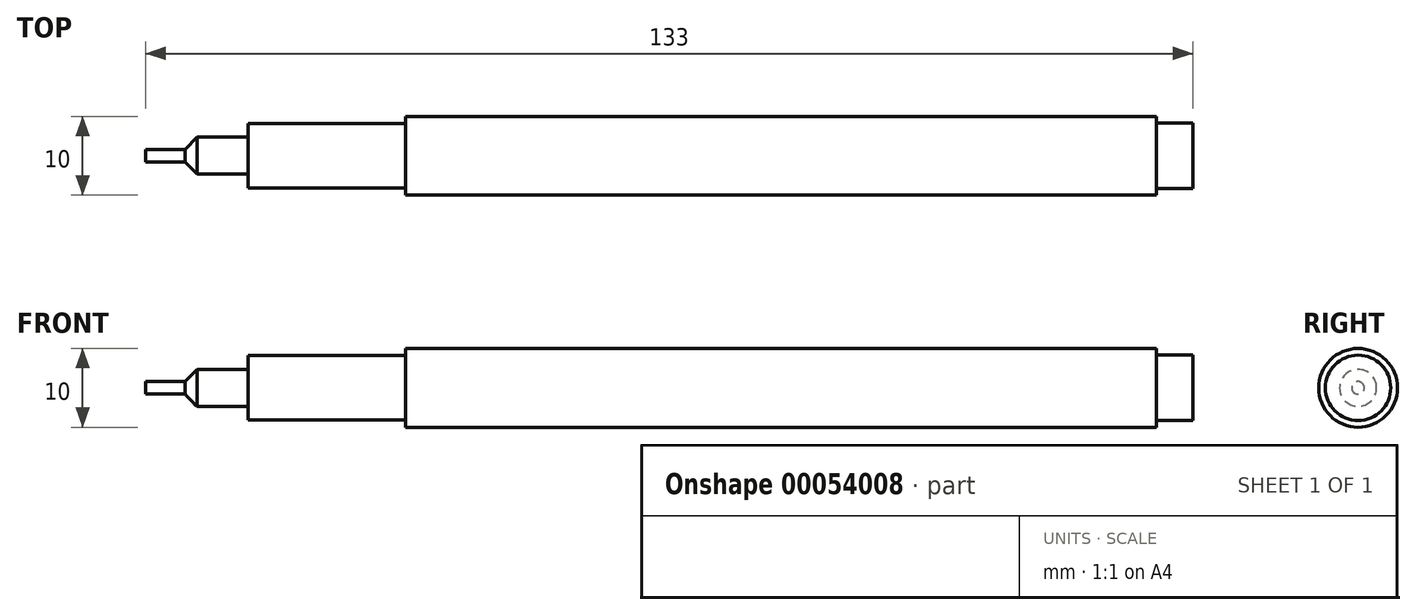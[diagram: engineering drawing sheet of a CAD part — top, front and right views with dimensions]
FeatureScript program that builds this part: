
annotation { "Feature Type Name" : "Feature", "Feature Type Description" : "" }
export const myFeature = defineFeature(function(context is Context, id is Id, definition is map)
    precondition{}
    {
        {
            var Q0;
            Q0=qCreatedBy(makeId("Top.planeOp"),FACE);
            var sketch = newSketch(context, id + "F0", { "sketchPlane" : qUnion([Q0])});
            skLineSegment(sketch, "E0", {"start": v(0, 0) * mm, "end": v(0, 0.8) * mm});
            skLineSegment(sketch, "E1", {"start": v(0, 0.8) * mm, "end": v(5, 0.8) * mm});
            skLineSegment(sketch, "E2", {"start": v(33, 4.1) * mm, "end": v(33, 5) * mm});
            skLineSegment(sketch, "E3", {"start": v(33, 5) * mm, "end": v(128.4, 5) * mm});
            skLineSegment(sketch, "E4", {"start": v(128.4, 5) * mm, "end": v(128.4, 4.15) * mm});
            skLineSegment(sketch, "E5", {"start": v(128.4, 4.15) * mm, "end": v(133, 4.15) * mm});
            skLineSegment(sketch, "E6", {"start": v(133, 4.15) * mm, "end": v(133, 0) * mm});
            skLineSegment(sketch, "E7", {"start": v(133, 0) * mm, "end": v(0, 0) * mm});
            skLineSegment(sketch, "E8", {"start": v(0, 0) * mm, "end": v(-10.28, 0) * mm, "construction": true});
            skLineSegment(sketch, "E9", {"start": v(33, 4.1) * mm, "end": v(13, 4.1) * mm});
            skLineSegment(sketch, "E10", {"start": v(13, 4.1) * mm, "end": v(13, 2.35) * mm});
            skLineSegment(sketch, "E11", {"start": v(13, 2.35) * mm, "end": v(6.5, 2.35) * mm});
            skLineSegment(sketch, "E12", {"start": v(6.5, 2.35) * mm, "end": v(5, 0.8) * mm});
            skSolve(sketch);
        }
        {
            var Q0;
            Q0=qSketchRegion(id+"F0",true);
            var Q1;
            Q1=sQuery(id+"F0.wireOp",EDGE,"E8");
            revolve(context, id + "F1", {"entities" : qUnion([Q0]), "axis" : qUnion([Q1]), "revolveType" : RevolveType.FULL});
        }
    });
